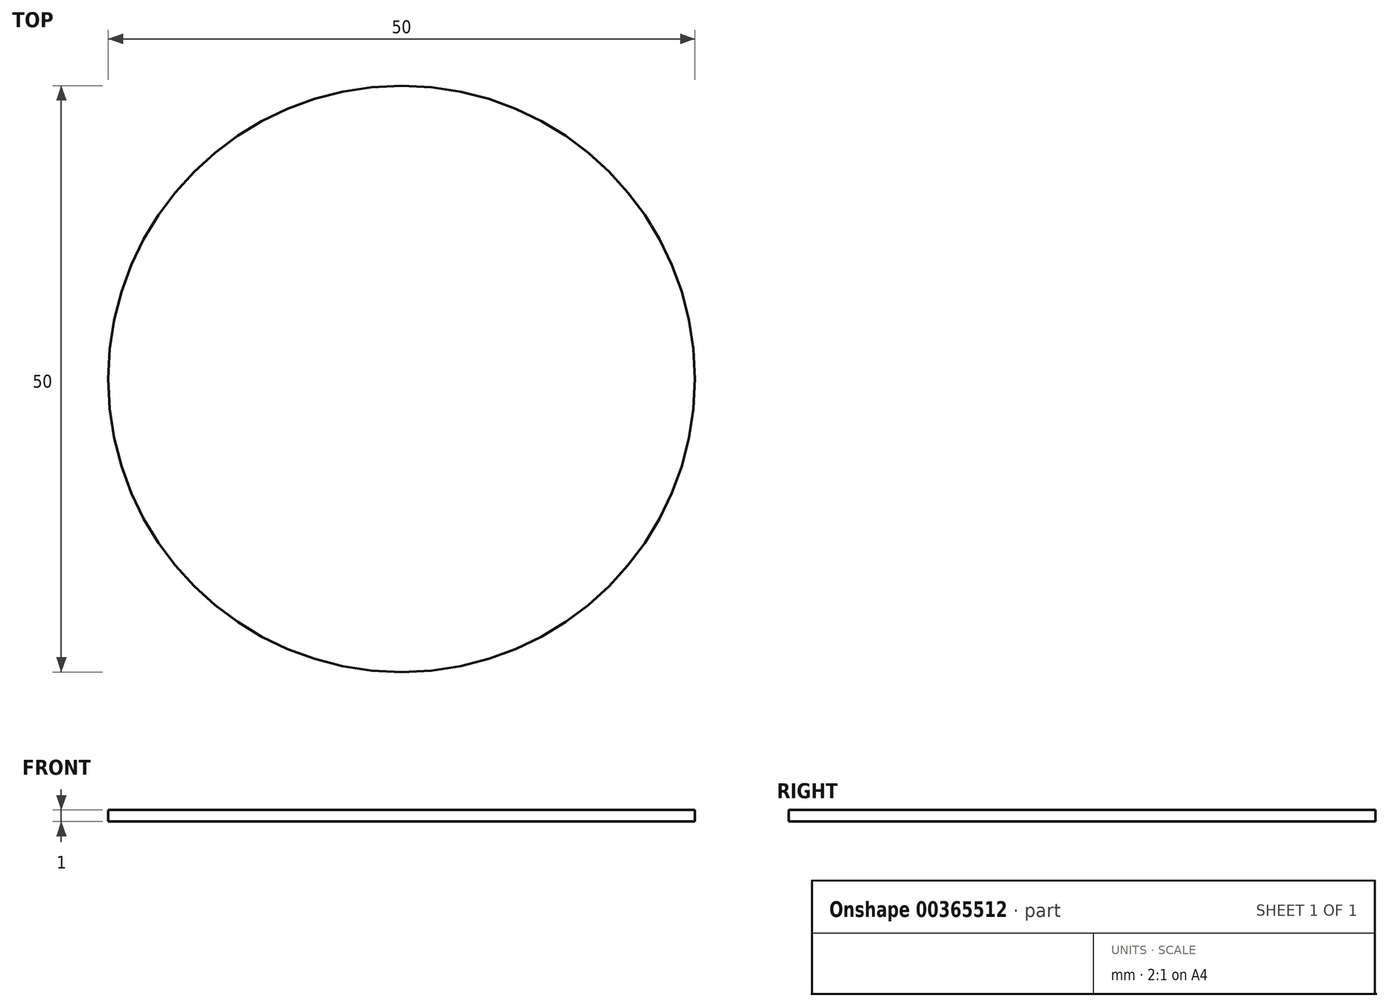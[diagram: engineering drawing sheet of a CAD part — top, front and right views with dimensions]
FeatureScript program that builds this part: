
annotation { "Feature Type Name" : "Feature", "Feature Type Description" : "" }
export const myFeature = defineFeature(function(context is Context, id is Id, definition is map)
    precondition{}
    {
        {
            var Q0;
            Q0=qCreatedBy(makeId("Top.planeOp"),FACE);
            var sketch = newSketch(context, id + "F0", { "sketchPlane" : qUnion([Q0])});
            skCircle(sketch, "E0", {"center": v(0, 0) * mm, "radius": 25 * mm});
            skSolve(sketch);
        }
        {
            var Q0;
            Q0=makeQuery(id+"F0.imprint","IMPRINT",FACE,{"disambiguationData":[TD([[makeQuery(id+"F0.imprint","IMPRINT",EDGE,{"derivedFrom":sQuery(id+"F0.wireOp",EDGE,"E0")}),1.0]])]});
            extrude(context, id + "F1", {"entities" : qUnion([Q0]), "depth" : 1 * mm});
        }
    });
